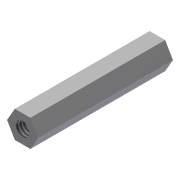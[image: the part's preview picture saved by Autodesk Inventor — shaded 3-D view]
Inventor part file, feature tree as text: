
AUTODESK INVENTOR PART (.ipt)
format: ipt  version: 2013 (Build 170138000, 138)  size: 80,896 bytes
history: native  units: in
note: dims shown in document units (in); Inventor stores cm internally (conversion verified against a paired STEP export)
features: sketch x2, extrude x1, hole x1, mirror x1
ambient origin geometry x8: Origin, YZ Plane, XZ Plane, XY Plane, X Axis, Y Axis, Z Axis, Center Point
bodies: Solid1 (feature_tree)
feature tree (5):
  extrude  "Extrusion1"  Depth=1.25in TaperAngle=0.0deg
  hole  "Hole1"  [1 undecoded]
  mirror  "Mirror1"
  sketch  "Sketch1"  dims[d0=0.25in d1=1.25in d2=0.0in]
  sketch  "Sketch2"  dims[d3=0.13in d4=0.375in d5=0.375in d6=0.25in d7=0.5635in d8=0.375in d9=0.0in]
note: 1 required parameter value undecoded (feature->parameter linkage not recoverable at this tier; creation-order binding heuristic only, values carry confidence <= 0.55)
